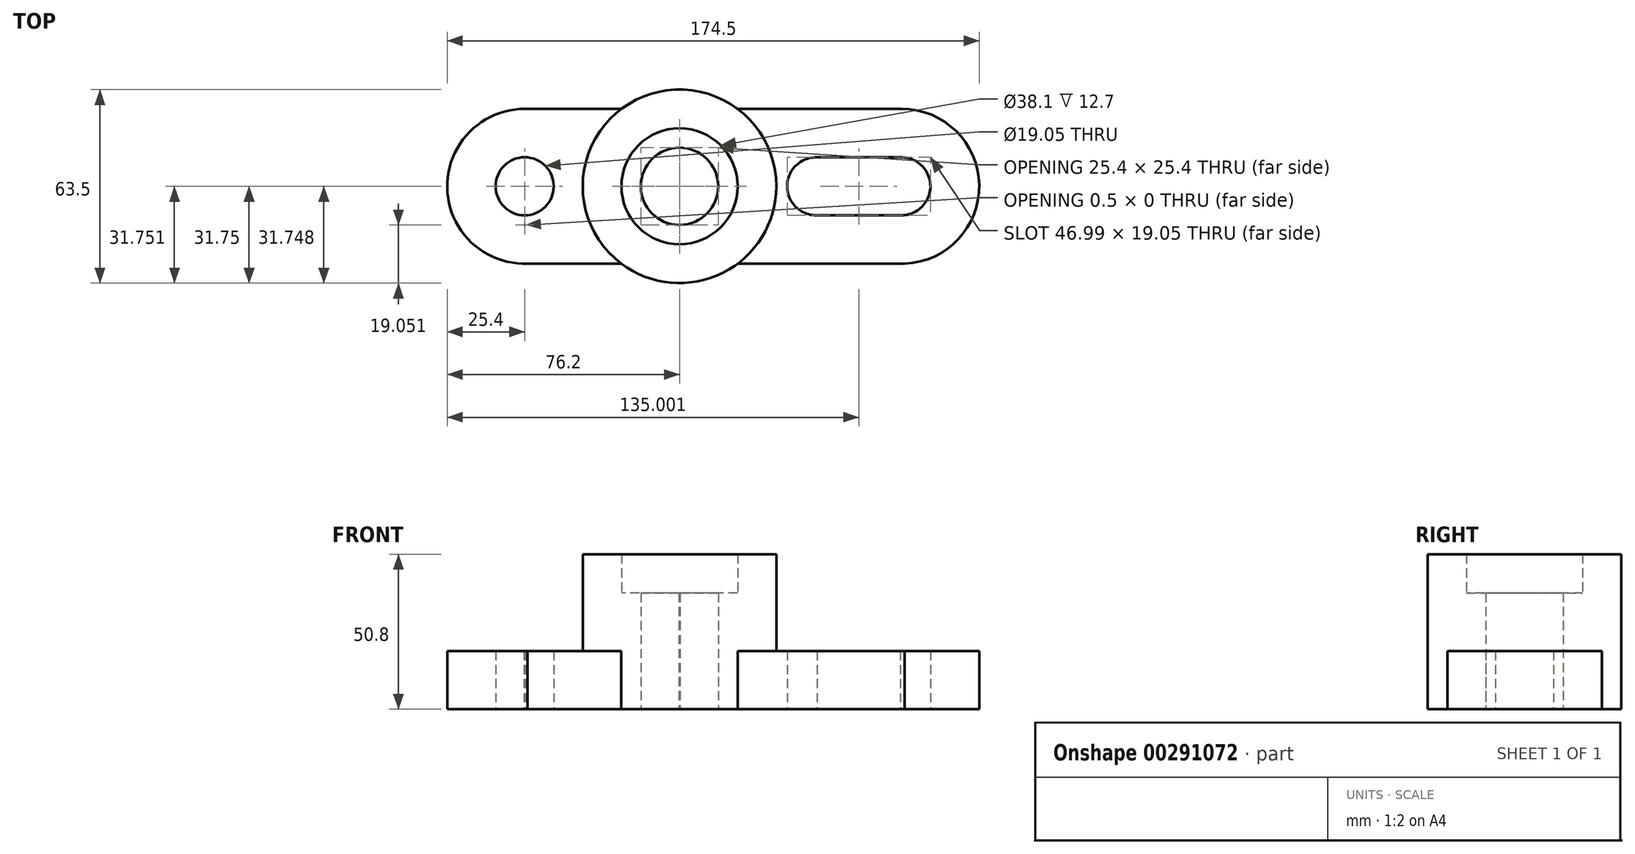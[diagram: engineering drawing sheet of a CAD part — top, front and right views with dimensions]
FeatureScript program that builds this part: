
annotation { "Feature Type Name" : "Feature", "Feature Type Description" : "" }
export const myFeature = defineFeature(function(context is Context, id is Id, definition is map)
    precondition{}
    {
        {
            var Q0;
            Q0=qCreatedBy(makeId("Top.planeOp"),FACE);
            var sketch = newSketch(context, id + "F0", { "sketchPlane" : qUnion([Q0])});
            skCircle(sketch, "E0", {"center": v(0, 0) * mm, "radius": 31.75 * mm});
            skCircle(sketch, "E1", {"center": v(0, 0) * mm, "radius": 19.05 * mm});
            skArc(sketch, "E2", {"start": v(0.2, -12.7) * mm, "mid": v(0, 12.7) * mm, "end": v(-0.2, -12.7) * mm});
            skArc(sketch, "E3", {"start": v(-51.05, -12.7) * mm, "mid": v(-50.8, -12.7) * mm, "end": v(-50.55, -12.7) * mm});
            skCircle(sketch, "E4", {"center": v(-50.8, 0) * mm, "radius": 9.53 * mm});
            skLineSegment(sketch, "E5", {"start": v(-51.05, -12.7) * mm, "end": v(-50.55, -12.7) * mm});
            skArc(sketch, "E6", {"start": v(45.1, 9.52) * mm, "mid": v(35.3, 0.14) * mm, "end": v(44.83, -9.53) * mm});
            skArc(sketch, "E7", {"start": v(72.77, -9.53) * mm, "mid": v(82.3, 0.14) * mm, "end": v(72.5, 9.52) * mm});
            skLineSegment(sketch, "E8", {"start": v(45.1, 9.52) * mm, "end": v(72.5, 9.52) * mm});
            skLineSegment(sketch, "E9", {"start": v(44.83, -9.53) * mm, "end": v(72.77, -9.53) * mm});
            skLineSegment(sketch, "E10.trimOffspring", {"start": v(-0.2, -12.7) * mm, "end": v(0.2, -12.7) * mm});
            skArc(sketch, "E11", {"start": v(-50.63, 25.4) * mm, "mid": v(-76.2, -0.4) * mm, "end": v(-49.82, -25.38) * mm});
            skArc(sketch, "E12", {"start": v(71.92, -25.38) * mm, "mid": v(98.3, -0.49) * mm, "end": v(72.9, 25.4) * mm});
            skLineSegment(sketch, "E13", {"start": v(-50.63, 25.4) * mm, "end": v(-19.05, 25.4) * mm});
            skLineSegment(sketch, "E14", {"start": v(-49.82, -25.38) * mm, "end": v(-19.08, -25.38) * mm});
            skLineSegment(sketch, "E15.trimOffspring", {"start": v(19.08, -25.38) * mm, "end": v(73.88, -25.38) * mm});
            skLineSegment(sketch, "E16.trimOffspring", {"start": v(19.05, 25.4) * mm, "end": v(72.9, 25.4) * mm});
            skSolve(sketch);
        }
        {
            var Q0;
            Q0=makeQuery(id+"F0.imprint","IMPRINT",FACE,{"disambiguationData":[TD([[makeQuery(id+"F0.imprint","IMPRINT",EDGE,{"derivedFrom":sQuery(id+"F0.wireOp",EDGE,"E1")}),-1.0]])]});
            extrude(context, id + "F1", {"entities" : qUnion([Q0]), "depth" : 50.8 * mm});
        }
        {
            var Q0;
            Q0=makeQuery(id+"F0.imprint","IMPRINT",FACE,{"disambiguationData":[TD([[makeQuery(id+"F0.imprint","IMPRINT",EDGE,{"derivedFrom":sQuery(id+"F0.wireOp",EDGE,"E1")}),1.0]])]});
            extrude(context, id + "F2", {"entities" : qUnion([Q0]), "operationType" : NewBodyOperationType.ADD, "depth" : 38.1 * mm});
        }
        {
            var Q0;
            Q0=makeQuery(id+"F0.imprint","IMPRINT",FACE,{"disambiguationData":[TD([[makeQuery(id+"F0.imprint","IMPRINT",EDGE,{"derivedFrom":sQuery(id+"F0.wireOp",EDGE,"E6")}),-1.0]])]});
            var Q1;
            Q1=makeQuery(id+"F0.imprint","IMPRINT",FACE,{"disambiguationData":[TD([[makeQuery(id+"F0.imprint","IMPRINT",EDGE,{"derivedFrom":sQuery(id+"F0.wireOp",EDGE,"E3")}),-1.0]])]});
            extrude(context, id + "F3", {"entities" : qUnion([Q0, Q1]), "operationType" : NewBodyOperationType.ADD, "depth" : 19.05 * mm});
        }
    });
